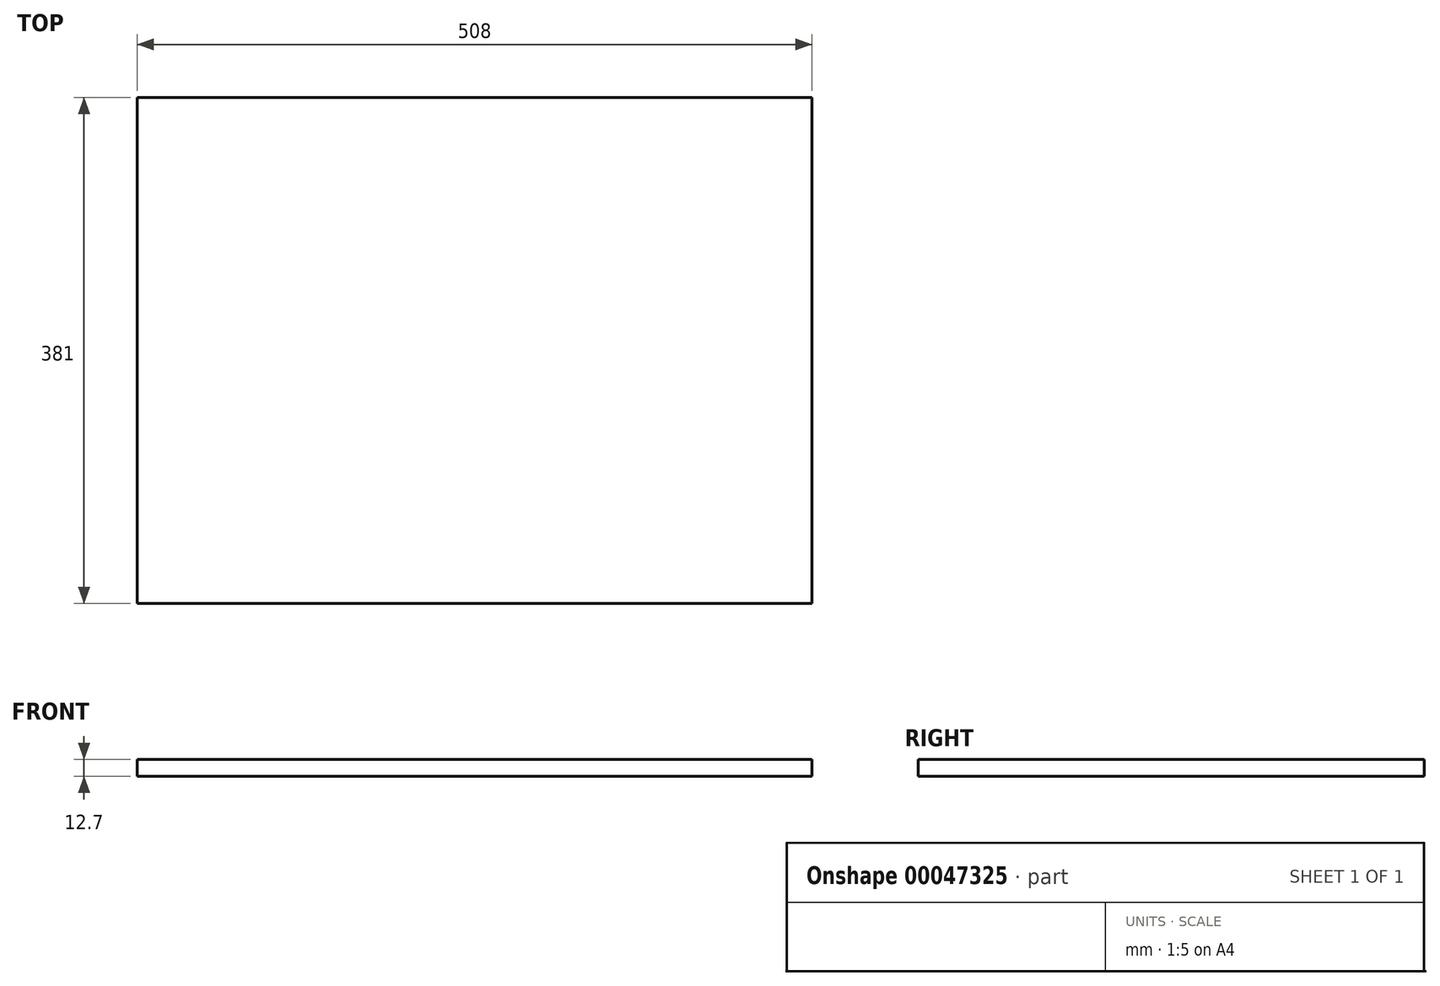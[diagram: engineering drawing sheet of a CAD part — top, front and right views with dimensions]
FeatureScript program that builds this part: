
annotation { "Feature Type Name" : "Feature", "Feature Type Description" : "" }
export const myFeature = defineFeature(function(context is Context, id is Id, definition is map)
    precondition{}
    {
        {
            var Q0;
            Q0=qCreatedBy(makeId("Top.planeOp"),FACE);
            var sketch = newSketch(context, id + "F0", { "sketchPlane" : qUnion([Q0])});
            skLineSegment(sketch, "E0.bottom", {"start": v(-57.49, 325.12) * mm, "end": v(450.51, 325.12) * mm});
            skLineSegment(sketch, "E0.top", {"start": v(-57.49, -55.88) * mm, "end": v(450.51, -55.88) * mm});
            skLineSegment(sketch, "E0.left", {"start": v(-57.49, 325.12) * mm, "end": v(-57.49, -55.88) * mm});
            skLineSegment(sketch, "E0.right", {"start": v(450.51, 325.12) * mm, "end": v(450.51, -55.88) * mm});
            skSolve(sketch);
        }
        {
            var Q0;
            Q0=makeQuery(id+"F0.imprint","IMPRINT",FACE,{"disambiguationData":[TD([[makeQuery(id+"F0.imprint","IMPRINT",EDGE,{"derivedFrom":sQuery(id+"F0.wireOp",EDGE,"E0.bottom")}),-1.0]])]});
            extrude(context, id + "F1", {"entities" : qUnion([Q0]), "depth" : 12.7 * mm});
        }
    });
